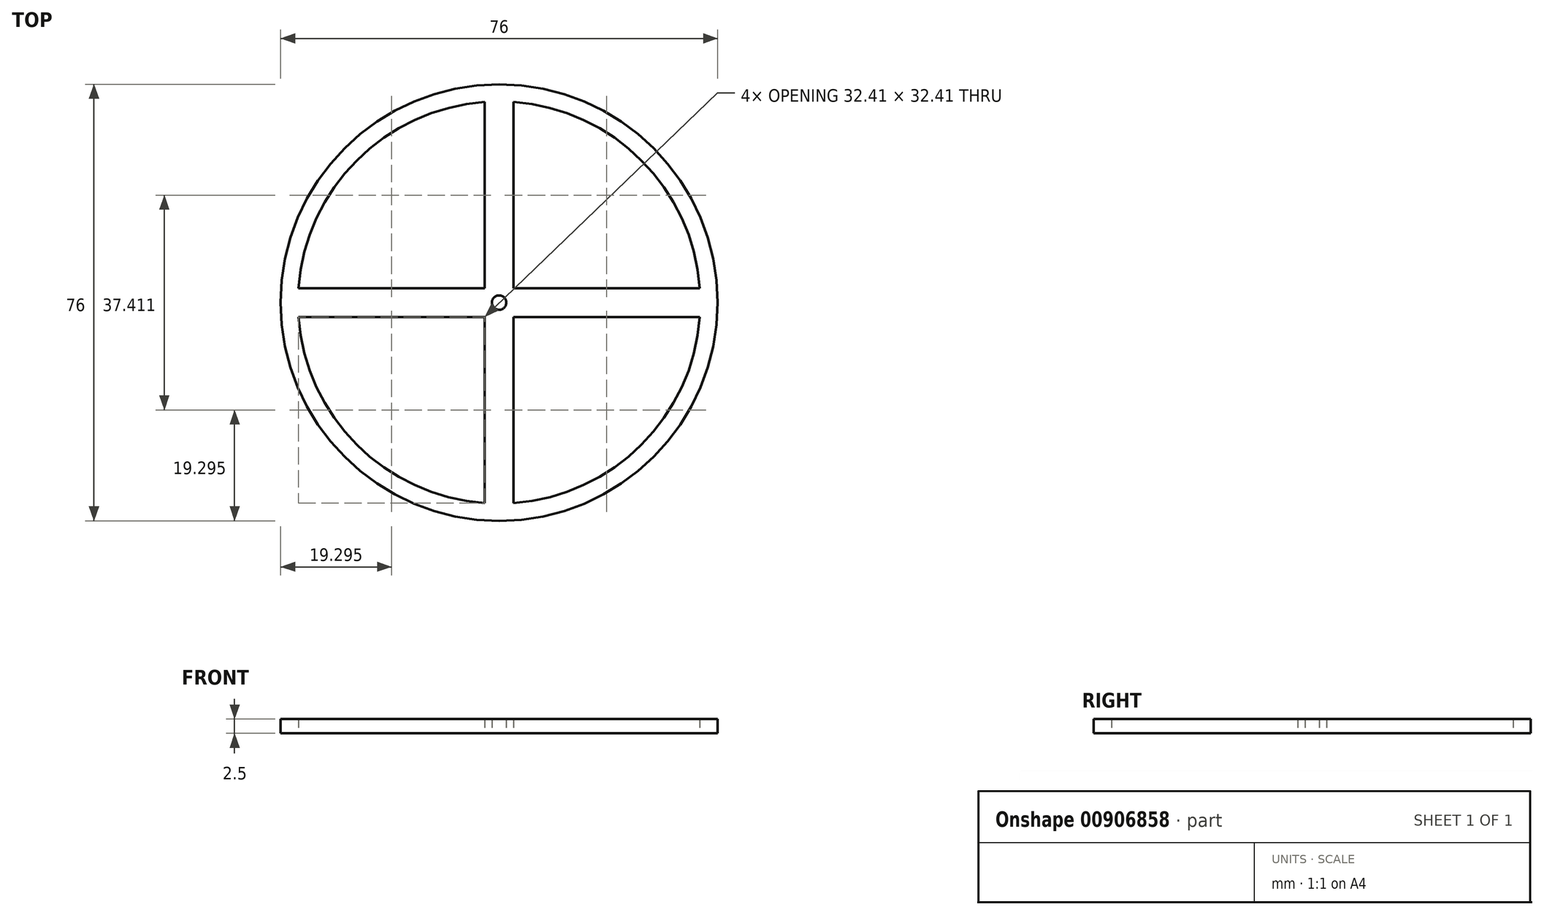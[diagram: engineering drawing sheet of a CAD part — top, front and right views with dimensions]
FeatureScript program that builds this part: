
annotation { "Feature Type Name" : "Feature", "Feature Type Description" : "" }
export const myFeature = defineFeature(function(context is Context, id is Id, definition is map)
    precondition{}
    {
        {
            var Q0;
            Q0=qCreatedBy(makeId("Top.planeOp"),FACE);
            var sketch = newSketch(context, id + "F0", { "sketchPlane" : qUnion([Q0])});
            skCircle(sketch, "E0", {"center": v(0, 0) * mm, "radius": 38 * mm});
            skArc(sketch, "E1", {"start": v(-2.5, 34.91) * mm, "mid": v(-24.75, 24.75) * mm, "end": v(-34.91, 2.5) * mm});
            skLineSegment(sketch, "E2.left", {"start": v(-2.5, 34.91) * mm, "end": v(-2.5, 2.5) * mm});
            skLineSegment(sketch, "E2.right", {"start": v(2.5, 34.91) * mm, "end": v(2.5, 2.5) * mm});
            skPoint(sketch, "E2.bottom.start.orphan", {"position": v(-2.5, 51.34) * mm});
            skPoint(sketch, "E3.orphan", {"position": v(2.5, 51.34) * mm});
            skPoint(sketch, "E4.right.start.orphan", {"position": v(-53.75, 3.8) * mm});
            skPoint(sketch, "E5.orphan", {"position": v(-53.75, -3.8) * mm});
            skLineSegment(sketch, "E6.trimOffspring", {"start": v(34.91, 2.5) * mm, "end": v(2.5, 2.5) * mm});
            skLineSegment(sketch, "E7.trimOffspring", {"start": v(-2.5, 2.5) * mm, "end": v(-34.91, 2.5) * mm});
            skLineSegment(sketch, "E8.trimOffspring", {"start": v(-2.5, -2.5) * mm, "end": v(-2.5, -34.91) * mm});
            skLineSegment(sketch, "E9.trimOffspring", {"start": v(-2.5, -2.5) * mm, "end": v(-34.91, -2.5) * mm});
            skLineSegment(sketch, "E10.trimOffspring", {"start": v(2.5, -2.5) * mm, "end": v(2.5, -34.91) * mm});
            skLineSegment(sketch, "E11.trimOffspring", {"start": v(34.91, -2.5) * mm, "end": v(2.5, -2.5) * mm});
            skPoint(sketch, "E4.left.end.orphan", {"position": v(53.75, -3.8) * mm});
            skPoint(sketch, "E4.left.start.orphan", {"position": v(53.75, 3.8) * mm});
            skArc(sketch, "E12.trimOffspring", {"start": v(2.5, -34.91) * mm, "mid": v(24.75, -24.75) * mm, "end": v(34.91, -2.5) * mm});
            skPoint(sketch, "E2.top.start.orphan", {"position": v(-2.5, -51.34) * mm});
            skPoint(sketch, "E13.orphan", {"position": v(2.5, -51.34) * mm});
            skArc(sketch, "E14.trimOffspring", {"start": v(-34.91, -2.5) * mm, "mid": v(-24.75, -24.75) * mm, "end": v(-2.5, -34.91) * mm});
            skArc(sketch, "E15.trimOffspring", {"start": v(34.91, 2.5) * mm, "mid": v(24.75, 24.75) * mm, "end": v(2.5, 34.91) * mm});
            skCircle(sketch, "E16", {"center": v(0, 0) * mm, "radius": 1.25 * mm});
            skSolve(sketch);
        }
        {
            var Q0;
            Q0 = qSketchRegion(id + "F0", true);
            extrude(context, id + "F1", {"entities" : qUnion([Q0]), "depth" : 2.5 * mm, "offsetDistance" : 25 * mm});
        }
    });
